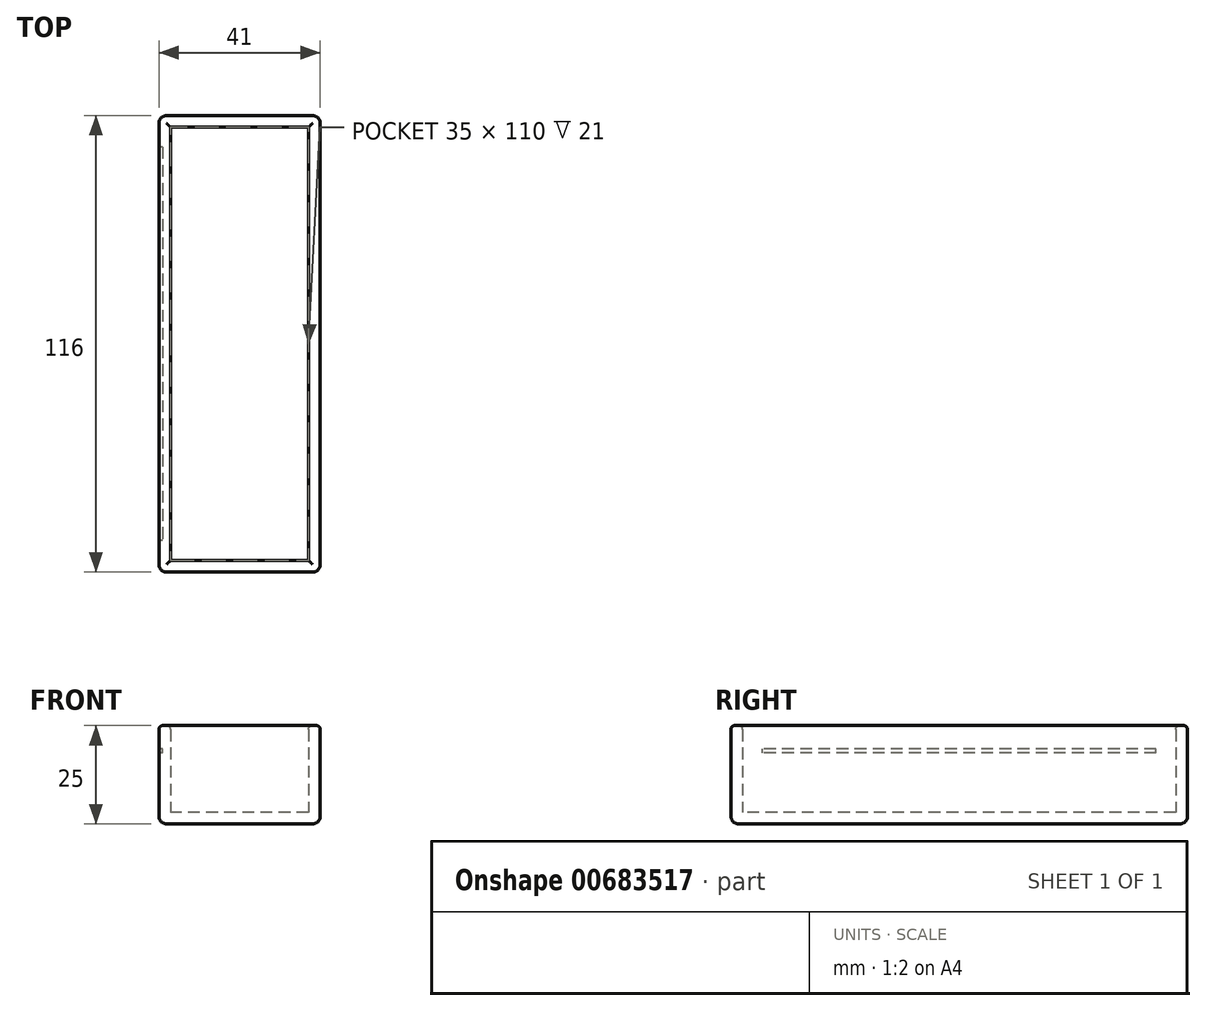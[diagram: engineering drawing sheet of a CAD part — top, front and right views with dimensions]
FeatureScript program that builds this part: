
annotation { "Feature Type Name" : "Feature", "Feature Type Description" : "" }
export const myFeature = defineFeature(function(context is Context, id is Id, definition is map)
    precondition{}
    {
        {
            var Q0;
            Q0=qCreatedBy(makeId("Top.planeOp"),FACE);
            var sketch = newSketch(context, id + "F0", { "sketchPlane" : qUnion([Q0])});
            skLineSegment(sketch, "E0.bottom", {"start": v(17.5, 55) * mm, "end": v(-17.5, 55) * mm});
            skLineSegment(sketch, "E0.top", {"start": v(17.5, -55) * mm, "end": v(-17.5, -55) * mm});
            skLineSegment(sketch, "E0.left", {"start": v(17.5, 55) * mm, "end": v(17.5, -55) * mm});
            skLineSegment(sketch, "E0.right", {"start": v(-17.5, 55) * mm, "end": v(-17.5, -55) * mm});
            skPoint(sketch, "E0.middle", {"position": v(0, 0) * mm});
            skSolve(sketch);
        }
        {
            var Q0;
            Q0 = qSketchRegion(id + "F0", true);
            extrude(context, id + "F1", {"entities" : qUnion([Q0]), "depth" : 3 * mm, "offsetDistance" : 25 * mm});
        }
        {
            var Q0;
            Q0=qCreatedBy(makeId("Top.planeOp"),FACE);
            var sketch = newSketch(context, id + "F2", { "sketchPlane" : qUnion([Q0])});
            skLineSegment(sketch, "E1.0", {"start": v(20.5, 58) * mm, "end": v(-20.5, 58) * mm});
            skLineSegment(sketch, "E1.1", {"start": v(20.5, 58) * mm, "end": v(20.5, -58) * mm});
            skLineSegment(sketch, "E1.2", {"start": v(20.5, -58) * mm, "end": v(-20.5, -58) * mm});
            skLineSegment(sketch, "E1.3", {"start": v(-20.5, 58) * mm, "end": v(-20.5, -58) * mm});
            skLineSegment(sketch, "E2.0", {"start": v(-17.5, 55) * mm, "end": v(-17.5, -55) * mm});
            skLineSegment(sketch, "E2.1", {"start": v(17.5, 55) * mm, "end": v(-17.5, 55) * mm});
            skLineSegment(sketch, "E2.2", {"start": v(17.5, 55) * mm, "end": v(17.5, -55) * mm});
            skLineSegment(sketch, "E2.3", {"start": v(17.5, -55) * mm, "end": v(-17.5, -55) * mm});
            skSolve(sketch);
        }
        {
            var Q0;
            Q0 = qSketchRegion(id + "F2", true);
            extrude(context, id + "F3", {"entities" : qUnion([Q0]), "operationType" : NewBodyOperationType.ADD, "depth" : 25 * mm, "offsetDistance" : 25 * mm});
        }
        {
            var Q0;
            Q0=makeQuery(id+"F3.opExtrude","CAP_FACE",FACE,{"disambiguationData":[OSD([sQuery(id+"F2.wireOp",EDGE,"E1.0"),sQuery(id+"F2.wireOp",EDGE,"E1.1"),sQuery(id+"F2.wireOp",EDGE,"E1.2"),sQuery(id+"F2.wireOp",EDGE,"E1.3"),sQuery(id+"F2.wireOp",EDGE,"E2.0"),sQuery(id+"F2.wireOp",EDGE,"E2.1"),sQuery(id+"F2.wireOp",EDGE,"E2.2"),sQuery(id+"F2.wireOp",EDGE,"E2.3")])],"isStart":false});
            fillet(context, id + "F4", {"entities" : qUnion([Q0]), "radius" : 1 * mm, "tangentPropagation" : true, "allowEdgeOverflow" : false});
        }
        {
            var Q0;
            Q0=makeQuery(id+"F3.opExtrude","SWEPT_EDGE",EDGE,{"disambiguationData":[OSD([sQuery(id+"F2.wireOp",EDGE,"E1.1"),sQuery(id+"F2.wireOp",EDGE,"E1.2")])]});
            var Q1;
            Q1=makeQuery(id+"F3.opExtrude","SWEPT_EDGE",EDGE,{"disambiguationData":[OSD([sQuery(id+"F2.wireOp",EDGE,"E1.2"),sQuery(id+"F2.wireOp",EDGE,"E1.3")])]});
            var Q2;
            Q2=makeQuery(id+"F3.opExtrude","SWEPT_EDGE",EDGE,{"disambiguationData":[OSD([sQuery(id+"F2.wireOp",EDGE,"E1.0"),sQuery(id+"F2.wireOp",EDGE,"E1.3")])]});
            var Q3;
            Q3=makeQuery(id+"F3.opExtrude","SWEPT_EDGE",EDGE,{"disambiguationData":[OSD([sQuery(id+"F2.wireOp",EDGE,"E1.0"),sQuery(id+"F2.wireOp",EDGE,"E1.1")])]});
            fillet(context, id + "F5", {"entities" : qUnion([Q0, Q1, Q2, Q3]), "radius" : 2 * mm, "tangentPropagation" : true, "allowEdgeOverflow" : false});
        }
        {
            var Q0;
            Q0=makeQuery(id+"F3.opExtrude","SWEPT_FACE",FACE,{"disambiguationData":[OSD([sQuery(id+"F2.wireOp",EDGE,"E1.3")])]});
            var sketch = newSketch(context, id + "F6", { "sketchPlane" : qUnion([Q0])});
            skText(sketch, "E3", { "text": "ДЛЯ ПОСУДЫ", "fontName": "RobotoSlab-Bold.ttf"});
            const initialGuessF6  = {"E3": [-0.0503, 0.00767, 1, 0, 0.01027]};
            skSetInitialGuess(sketch, initialGuessF6);
            skSolve(sketch);
        }
        {
            var Q0;
            Q0=makeQuery(id+"F6.imprint","IMPRINT",FACE,{"disambiguationData":[TD([[makeQuery(id+"F6.imprint","IMPRINT",EDGE,{"derivedFrom":sQuery(id+"F6.wireOp",EDGE,"E3.sketch_text.stroke-0")}),1.0]])]});
            var sketch = newSketch(context, id + "F7", { "sketchPlane" : qUnion([Q0])});
            skLineSegment(sketch, "E4.bottom", {"start": v(-50.03, 18.12) * mm, "end": v(49.97, 18.12) * mm});
            skLineSegment(sketch, "E4.top", {"start": v(-50.03, 19.12) * mm, "end": v(49.97, 19.12) * mm});
            skLineSegment(sketch, "E4.left", {"start": v(-50.03, 18.12) * mm, "end": v(-50.03, 19.12) * mm});
            skLineSegment(sketch, "E4.right", {"start": v(49.97, 18.12) * mm, "end": v(49.97, 19.12) * mm});
            skSolve(sketch);
        }
        {
            var Q0;
            Q0 = qSketchRegion(id + "F7", true);
            extrude(context, id + "F8", {"entities" : qUnion([Q0]), "operationType" : NewBodyOperationType.REMOVE, "oppositeDirection" : true, "depth" : 1 * mm, "offsetDistance" : 25 * mm});
        }
        {
            var Q0;
            Q0=makeQuery(id+"F3.boolean.opBoolean","MERGE",FACE,{"derivedFrom":[makeQuery(id+"F1.opExtrude","CAP_FACE",FACE,{"disambiguationData":[OSD([sQuery(id+"F0.wireOp",EDGE,"E0.bottom"),sQuery(id+"F0.wireOp",EDGE,"E0.top"),sQuery(id+"F0.wireOp",EDGE,"E0.left"),sQuery(id+"F0.wireOp",EDGE,"E0.right")])],"isStart":true}),makeQuery(id+"F3.opExtrude","CAP_FACE",FACE,{"disambiguationData":[OSD([sQuery(id+"F2.wireOp",EDGE,"E1.0"),sQuery(id+"F2.wireOp",EDGE,"E1.1"),sQuery(id+"F2.wireOp",EDGE,"E1.2"),sQuery(id+"F2.wireOp",EDGE,"E1.3"),sQuery(id+"F2.wireOp",EDGE,"E2.0"),sQuery(id+"F2.wireOp",EDGE,"E2.1"),sQuery(id+"F2.wireOp",EDGE,"E2.2"),sQuery(id+"F2.wireOp",EDGE,"E2.3")])],"isStart":true})]});
            fillet(context, id + "F9", {"entities" : qUnion([Q0]), "radius" : 2 * mm, "tangentPropagation" : true, "allowEdgeOverflow" : false});
        }
    });
